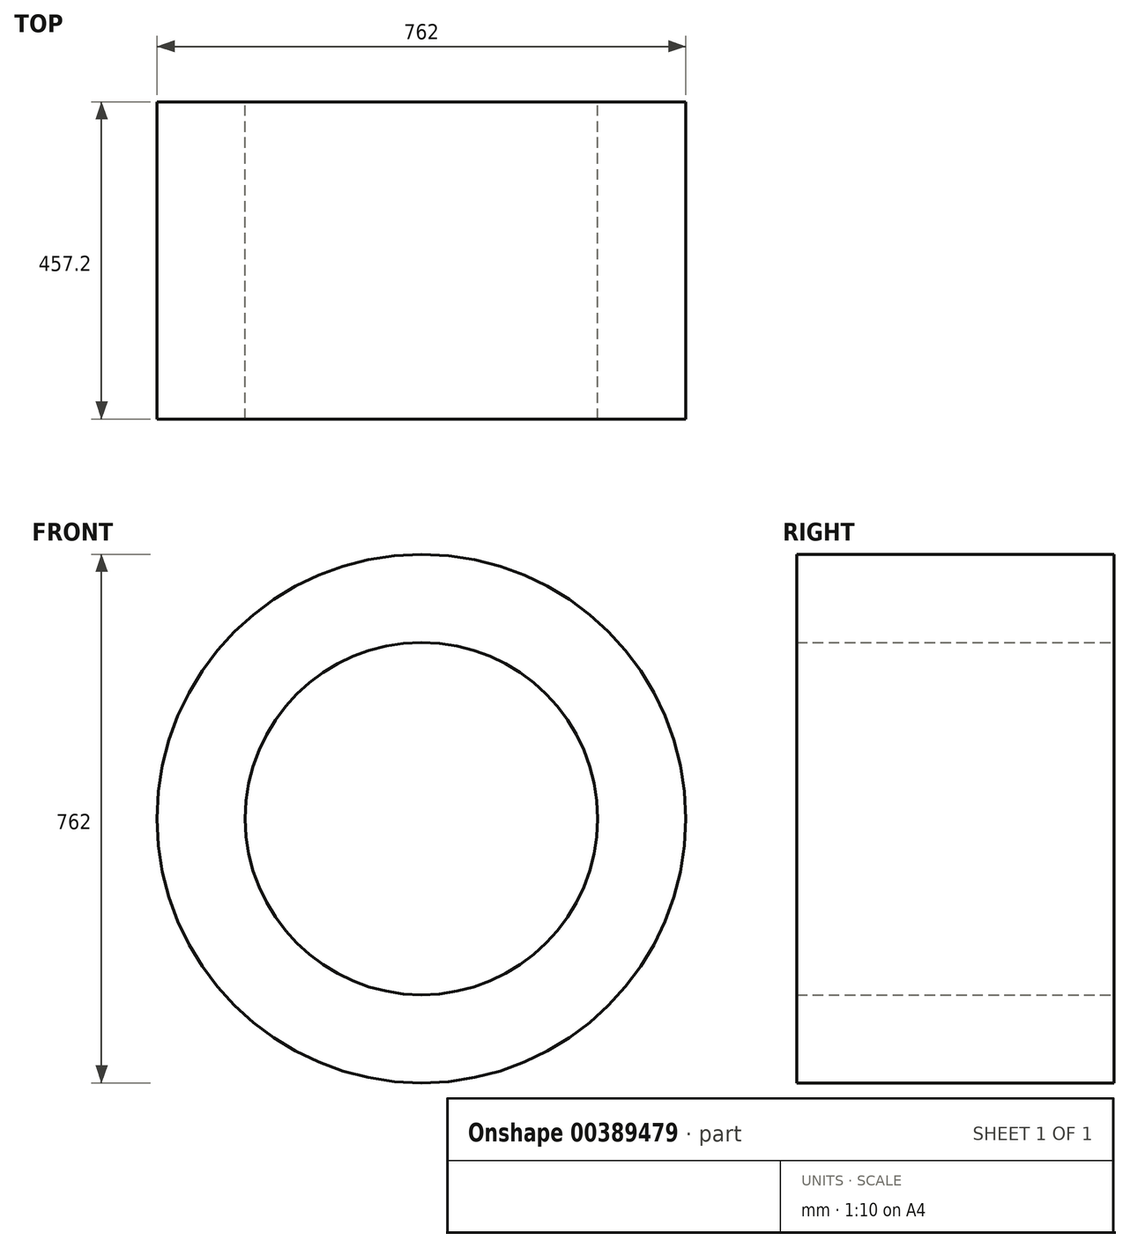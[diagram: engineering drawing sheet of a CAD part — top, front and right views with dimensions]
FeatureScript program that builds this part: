
annotation { "Feature Type Name" : "Feature", "Feature Type Description" : "" }
export const myFeature = defineFeature(function(context is Context, id is Id, definition is map)
    precondition{}
    {
        {
            var Q0;
            Q0=qCreatedBy(makeId("Front.planeOp"),FACE);
            var sketch = newSketch(context, id + "F0", { "sketchPlane" : qUnion([Q0])});
            skCircle(sketch, "E0", {"center": v(0, 0) * mm, "radius": 381 * mm});
            skCircle(sketch, "E1", {"center": v(0, 0) * mm, "radius": 254 * mm});
            skSolve(sketch);
        }
        {
            var Q0;
            Q0 = qSketchRegion(id + "F0", true);
            extrude(context, id + "F1", {"entities" : qUnion([Q0]), "depth" : 457.2 * mm});
        }
    });
